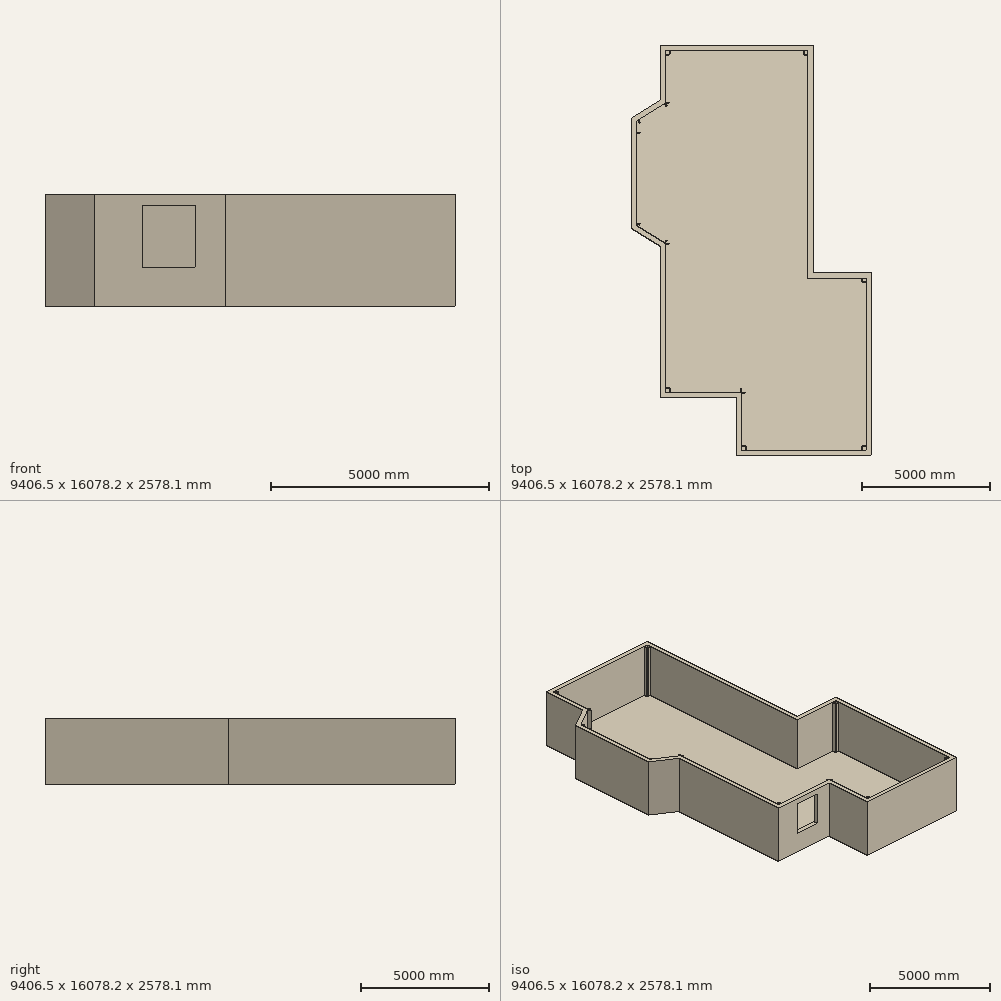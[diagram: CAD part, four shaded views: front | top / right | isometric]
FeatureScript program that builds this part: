
annotation { "Feature Type Name" : "Feature", "Feature Type Description" : "" }
export const myFeature = defineFeature(function(context is Context, id is Id, definition is map)
    precondition{}
    {
        {
            var Q0;
            Q0=qCreatedBy(makeId("Top.planeOp"),FACE);
            var sketch = newSketch(context, id + "F0", { "sketchPlane" : qUnion([Q0])});
            skLineSegment(sketch, "E0", {"start": v(-8280.4, 16078.2) * mm, "end": v(-2286, 16078.2) * mm});
            skLineSegment(sketch, "E1", {"start": v(-2286, 16078.2) * mm, "end": v(-2286, 7162.8) * mm});
            skLineSegment(sketch, "E2", {"start": v(-2286, 7162.8) * mm, "end": v(0, 7162.8) * mm});
            skLineSegment(sketch, "E3", {"start": v(0, 7162.8) * mm, "end": v(0, 0) * mm});
            skLineSegment(sketch, "E4", {"start": v(0, 0) * mm, "end": v(-5283.2, 0) * mm});
            skLineSegment(sketch, "E5", {"start": v(-5283.2, 0) * mm, "end": v(-5283.2, 2286) * mm});
            skLineSegment(sketch, "E6", {"start": v(-5283.2, 2286) * mm, "end": v(-8280.4, 2286) * mm});
            skLineSegment(sketch, "E7", {"start": v(-8280.4, 2286) * mm, "end": v(-8280.4, 8201.03) * mm});
            skLineSegment(sketch, "E8", {"start": v(-8280.4, 8201.03) * mm, "end": v(-9406.5, 8900.32) * mm});
            skLineSegment(sketch, "E9", {"start": v(-9406.5, 8900.32) * mm, "end": v(-9406.5, 13223.08) * mm});
            skLineSegment(sketch, "E10", {"start": v(-9406.5, 13223.08) * mm, "end": v(-8280.4, 13922.38) * mm});
            skLineSegment(sketch, "E11", {"start": v(-8280.4, 13922.38) * mm, "end": v(-8280.4, 16078.2) * mm});
            skSolve(sketch);
        }
        {
            var Q0;
            Q0 = qSketchRegion(id + "F0", true);
            extrude(context, id + "F1", {"entities" : qUnion([Q0]), "depth" : 2578.1 * mm});
        }
        {
            var Q0;
            Q0=makeQuery(id+"F1.opExtrude","CAP_FACE",FACE,{"disambiguationData":[OSD([sQuery(id+"F0.wireOp",EDGE,"E0"),sQuery(id+"F0.wireOp",EDGE,"E1"),sQuery(id+"F0.wireOp",EDGE,"E2"),sQuery(id+"F0.wireOp",EDGE,"E3"),sQuery(id+"F0.wireOp",EDGE,"E4"),sQuery(id+"F0.wireOp",EDGE,"E5"),sQuery(id+"F0.wireOp",EDGE,"E6"),sQuery(id+"F0.wireOp",EDGE,"E7"),sQuery(id+"F0.wireOp",EDGE,"E8"),sQuery(id+"F0.wireOp",EDGE,"E9"),sQuery(id+"F0.wireOp",EDGE,"E10"),sQuery(id+"F0.wireOp",EDGE,"E11")])],"isStart":false});
            shell(context, id + "F2", {"entities" : qUnion([Q0]), "thickness" : 203.2 * mm});
        }
        {
            var Q0;
            Q0=makeQuery(id+"F2.opShell","OFFSET_FACE",FACE,{"disambiguationData":[OSD([sQuery(id+"F0.wireOp",EDGE,"E6")])]});
            var sketch = newSketch(context, id + "F3", { "sketchPlane" : qUnion([Q0])});
            skLineSegment(sketch, "E12.bottom", {"start": v(5969, 2324.1) * mm, "end": v(7188.2, 2324.1) * mm});
            skLineSegment(sketch, "E12.top", {"start": v(5969, 901.7) * mm, "end": v(7188.2, 901.7) * mm});
            skLineSegment(sketch, "E12.left", {"start": v(5969, 2324.1) * mm, "end": v(5969, 901.7) * mm});
            skLineSegment(sketch, "E12.right", {"start": v(7188.2, 2324.1) * mm, "end": v(7188.2, 901.7) * mm});
            skPoint(sketch, "E13", {"position": v(6578.6, 2324.1) * mm});
            skSolve(sketch);
        }
        {
            var Q0;
            Q0=makeQuery(id+"F2.opShell","OFFSET_FACE",FACE,{"disambiguationData":[OSD([sQuery(id+"F0.wireOp",EDGE,"E0"),sQuery(id+"F0.wireOp",EDGE,"E1"),sQuery(id+"F0.wireOp",EDGE,"E2"),sQuery(id+"F0.wireOp",EDGE,"E3"),sQuery(id+"F0.wireOp",EDGE,"E4"),sQuery(id+"F0.wireOp",EDGE,"E5"),sQuery(id+"F0.wireOp",EDGE,"E6"),sQuery(id+"F0.wireOp",EDGE,"E7"),sQuery(id+"F0.wireOp",EDGE,"E8"),sQuery(id+"F0.wireOp",EDGE,"E9"),sQuery(id+"F0.wireOp",EDGE,"E10"),sQuery(id+"F0.wireOp",EDGE,"E11")])]});
            var sketch = newSketch(context, id + "F4", { "sketchPlane" : qUnion([Q0])});
            skLineSegment(sketch, "E14.bottom", {"start": v(-8077.2, 13811.9) * mm, "end": v(-7937.5, 13811.9) * mm});
            skLineSegment(sketch, "E14.top", {"start": v(-8077.2, 13850) * mm, "end": v(-7937.5, 13850) * mm});
            skLineSegment(sketch, "E14.left", {"start": v(-8077.2, 13811.9) * mm, "end": v(-8077.2, 13850) * mm});
            skLineSegment(sketch, "E14.right", {"start": v(-7937.5, 13811.9) * mm, "end": v(-7937.5, 13850) * mm});
            skLineSegment(sketch, "E15.bottom", {"start": v(-7934.96, 15875) * mm, "end": v(-7896.86, 15875) * mm});
            skLineSegment(sketch, "E15.top", {"start": v(-7934.96, 15735.3) * mm, "end": v(-7896.86, 15735.3) * mm});
            skLineSegment(sketch, "E15.left", {"start": v(-7934.96, 15875) * mm, "end": v(-7934.96, 15735.3) * mm});
            skLineSegment(sketch, "E15.right", {"start": v(-7896.86, 15875) * mm, "end": v(-7896.86, 15735.3) * mm});
            skLineSegment(sketch, "E16.bottom", {"start": v(-8077.2, 15694.66) * mm, "end": v(-7937.5, 15694.66) * mm});
            skLineSegment(sketch, "E16.top", {"start": v(-8077.2, 15732.76) * mm, "end": v(-7937.5, 15732.76) * mm});
            skLineSegment(sketch, "E16.left", {"start": v(-8077.2, 15694.66) * mm, "end": v(-8077.2, 15732.76) * mm});
            skLineSegment(sketch, "E16.right", {"start": v(-7937.5, 15694.66) * mm, "end": v(-7937.5, 15732.76) * mm});
            skLineSegment(sketch, "E17.bottom", {"start": v(-2631.44, 15875) * mm, "end": v(-2669.54, 15875) * mm});
            skLineSegment(sketch, "E17.top", {"start": v(-2631.44, 15735.3) * mm, "end": v(-2669.54, 15735.3) * mm});
            skLineSegment(sketch, "E17.left", {"start": v(-2631.44, 15875) * mm, "end": v(-2631.44, 15735.3) * mm});
            skLineSegment(sketch, "E17.right", {"start": v(-2669.54, 15875) * mm, "end": v(-2669.54, 15735.3) * mm});
            skLineSegment(sketch, "E18.bottom", {"start": v(-2489.2, 15694.66) * mm, "end": v(-2628.9, 15694.66) * mm});
            skLineSegment(sketch, "E18.top", {"start": v(-2489.2, 15732.76) * mm, "end": v(-2628.9, 15732.76) * mm});
            skLineSegment(sketch, "E18.left", {"start": v(-2489.2, 15694.66) * mm, "end": v(-2489.2, 15732.76) * mm});
            skLineSegment(sketch, "E18.right", {"start": v(-2628.9, 15694.66) * mm, "end": v(-2628.9, 15732.76) * mm});
            skLineSegment(sketch, "E19", {"start": v(-8078.22, 13808.73) * mm, "end": v(-8110.59, 13788.64) * mm});
            skLineSegment(sketch, "E20", {"start": v(-8110.59, 13788.64) * mm, "end": v(-8036.89, 13669.96) * mm});
            skLineSegment(sketch, "E21", {"start": v(-8036.89, 13669.96) * mm, "end": v(-8004.52, 13690.06) * mm});
            skLineSegment(sketch, "E22", {"start": v(-8004.52, 13690.06) * mm, "end": v(-8078.22, 13808.73) * mm});
            skLineSegment(sketch, "E23.bottom", {"start": v(-9203.3, 12669.47) * mm, "end": v(-9063.6, 12669.47) * mm});
            skLineSegment(sketch, "E23.top", {"start": v(-9203.3, 12631.37) * mm, "end": v(-9063.6, 12631.37) * mm});
            skLineSegment(sketch, "E23.left", {"start": v(-9203.3, 12669.47) * mm, "end": v(-9203.3, 12631.37) * mm});
            skLineSegment(sketch, "E23.right", {"start": v(-9063.6, 12669.47) * mm, "end": v(-9063.6, 12631.37) * mm});
            skLineSegment(sketch, "E24", {"start": v(-9162.3, 13135.53) * mm, "end": v(-9129.94, 13155.63) * mm});
            skLineSegment(sketch, "E25", {"start": v(-9129.94, 13155.63) * mm, "end": v(-9056.24, 13036.95) * mm});
            skLineSegment(sketch, "E26", {"start": v(-9056.24, 13036.95) * mm, "end": v(-9088.6, 13016.85) * mm});
            skLineSegment(sketch, "E27", {"start": v(-9088.6, 13016.85) * mm, "end": v(-9162.3, 13135.53) * mm});
            skLineSegment(sketch, "E28", {"start": v(-9162.3, 8987.87) * mm, "end": v(-9088.6, 9106.55) * mm});
            skLineSegment(sketch, "E29", {"start": v(-9088.6, 9106.55) * mm, "end": v(-9056.24, 9086.45) * mm});
            skLineSegment(sketch, "E30", {"start": v(-9056.24, 9086.45) * mm, "end": v(-9129.94, 8967.77) * mm});
            skLineSegment(sketch, "E31", {"start": v(-9129.94, 8967.77) * mm, "end": v(-9162.3, 8987.87) * mm});
            skLineSegment(sketch, "E32", {"start": v(-8109.57, 8334.13) * mm, "end": v(-8077.2, 8314.03) * mm});
            skLineSegment(sketch, "E33", {"start": v(-8077.2, 8314.03) * mm, "end": v(-8003.5, 8432.71) * mm});
            skLineSegment(sketch, "E34", {"start": v(-8003.5, 8432.71) * mm, "end": v(-8035.87, 8452.81) * mm});
            skLineSegment(sketch, "E35", {"start": v(-8035.87, 8452.81) * mm, "end": v(-8109.57, 8334.13) * mm});
            skLineSegment(sketch, "E36.bottom", {"start": v(-9203.3, 9061.59) * mm, "end": v(-9063.6, 9061.59) * mm});
            skLineSegment(sketch, "E36.top", {"start": v(-9203.3, 9099.69) * mm, "end": v(-9063.6, 9099.69) * mm});
            skLineSegment(sketch, "E36.left", {"start": v(-9203.3, 9061.59) * mm, "end": v(-9203.3, 9099.69) * mm});
            skLineSegment(sketch, "E36.right", {"start": v(-9063.6, 9061.59) * mm, "end": v(-9063.6, 9099.69) * mm});
            skLineSegment(sketch, "E37.bottom", {"start": v(-8077.2, 8311.5) * mm, "end": v(-7937.5, 8311.5) * mm});
            skLineSegment(sketch, "E37.top", {"start": v(-8077.2, 8273.4) * mm, "end": v(-7937.5, 8273.4) * mm});
            skLineSegment(sketch, "E37.left", {"start": v(-8077.2, 8311.5) * mm, "end": v(-8077.2, 8273.4) * mm});
            skLineSegment(sketch, "E37.right", {"start": v(-7937.5, 8311.5) * mm, "end": v(-7937.5, 8273.4) * mm});
            skLineSegment(sketch, "E38.bottom", {"start": v(-8077.2, 2631.44) * mm, "end": v(-7937.5, 2631.44) * mm});
            skLineSegment(sketch, "E38.top", {"start": v(-8077.2, 2669.54) * mm, "end": v(-7937.5, 2669.54) * mm});
            skLineSegment(sketch, "E38.left", {"start": v(-8077.2, 2631.44) * mm, "end": v(-8077.2, 2669.54) * mm});
            skLineSegment(sketch, "E38.right", {"start": v(-7937.5, 2631.44) * mm, "end": v(-7937.5, 2669.54) * mm});
            skLineSegment(sketch, "E39.bottom", {"start": v(-7896.86, 2489.2) * mm, "end": v(-7934.96, 2489.2) * mm});
            skLineSegment(sketch, "E39.top", {"start": v(-7896.86, 2628.9) * mm, "end": v(-7934.96, 2628.9) * mm});
            skLineSegment(sketch, "E39.left", {"start": v(-7896.86, 2489.2) * mm, "end": v(-7896.86, 2628.9) * mm});
            skLineSegment(sketch, "E39.right", {"start": v(-7934.96, 2489.2) * mm, "end": v(-7934.96, 2628.9) * mm});
            skLineSegment(sketch, "E40.bottom", {"start": v(-5082.54, 2489.2) * mm, "end": v(-5120.64, 2489.2) * mm});
            skLineSegment(sketch, "E40.top", {"start": v(-5082.54, 2628.9) * mm, "end": v(-5120.64, 2628.9) * mm});
            skLineSegment(sketch, "E40.left", {"start": v(-5082.54, 2489.2) * mm, "end": v(-5082.54, 2628.9) * mm});
            skLineSegment(sketch, "E40.right", {"start": v(-5120.64, 2489.2) * mm, "end": v(-5120.64, 2628.9) * mm});
            skLineSegment(sketch, "E41.top", {"start": v(-5080, 2448.56) * mm, "end": v(-4940.3, 2448.56) * mm});
            skLineSegment(sketch, "E41.right", {"start": v(-4940.3, 2486.66) * mm, "end": v(-4940.3, 2448.56) * mm});
            skLineSegment(sketch, "E42.bottom", {"start": v(-5080, 345.44) * mm, "end": v(-4940.3, 345.44) * mm});
            skLineSegment(sketch, "E42.top", {"start": v(-5080, 383.54) * mm, "end": v(-4940.3, 383.54) * mm});
            skLineSegment(sketch, "E42.left", {"start": v(-5080, 345.44) * mm, "end": v(-5080, 383.54) * mm});
            skLineSegment(sketch, "E42.right", {"start": v(-4940.3, 345.44) * mm, "end": v(-4940.3, 383.54) * mm});
            skLineSegment(sketch, "E43.bottom", {"start": v(-4937.76, 203.2) * mm, "end": v(-4899.66, 203.2) * mm});
            skLineSegment(sketch, "E43.top", {"start": v(-4937.76, 342.9) * mm, "end": v(-4899.66, 342.9) * mm});
            skLineSegment(sketch, "E43.left", {"start": v(-4937.76, 203.2) * mm, "end": v(-4937.76, 342.9) * mm});
            skLineSegment(sketch, "E43.right", {"start": v(-4899.66, 203.2) * mm, "end": v(-4899.66, 342.9) * mm});
            skLineSegment(sketch, "E44.bottom", {"start": v(-383.54, 203.2) * mm, "end": v(-345.44, 203.2) * mm});
            skLineSegment(sketch, "E44.top", {"start": v(-383.54, 342.9) * mm, "end": v(-345.44, 342.9) * mm});
            skLineSegment(sketch, "E44.left", {"start": v(-383.54, 203.2) * mm, "end": v(-383.54, 342.9) * mm});
            skLineSegment(sketch, "E44.right", {"start": v(-345.44, 203.2) * mm, "end": v(-345.44, 342.9) * mm});
            skLineSegment(sketch, "E45.bottom", {"start": v(-203.2, 345.44) * mm, "end": v(-342.9, 345.44) * mm});
            skLineSegment(sketch, "E45.top", {"start": v(-203.2, 383.54) * mm, "end": v(-342.9, 383.54) * mm});
            skLineSegment(sketch, "E45.left", {"start": v(-203.2, 345.44) * mm, "end": v(-203.2, 383.54) * mm});
            skLineSegment(sketch, "E45.right", {"start": v(-342.9, 345.44) * mm, "end": v(-342.9, 383.54) * mm});
            skLineSegment(sketch, "E46.bottom", {"start": v(-203.2, 6779.26) * mm, "end": v(-342.9, 6779.26) * mm});
            skLineSegment(sketch, "E46.top", {"start": v(-203.2, 6817.36) * mm, "end": v(-342.9, 6817.36) * mm});
            skLineSegment(sketch, "E46.left", {"start": v(-203.2, 6779.26) * mm, "end": v(-203.2, 6817.36) * mm});
            skLineSegment(sketch, "E46.right", {"start": v(-342.9, 6779.26) * mm, "end": v(-342.9, 6817.36) * mm});
            skLineSegment(sketch, "E47.bottom", {"start": v(-345.44, 6959.6) * mm, "end": v(-383.54, 6959.6) * mm});
            skLineSegment(sketch, "E47.top", {"start": v(-345.44, 6819.9) * mm, "end": v(-383.54, 6819.9) * mm});
            skLineSegment(sketch, "E47.left", {"start": v(-345.44, 6959.6) * mm, "end": v(-345.44, 6819.9) * mm});
            skLineSegment(sketch, "E47.right", {"start": v(-383.54, 6959.6) * mm, "end": v(-383.54, 6819.9) * mm});
            skLineSegment(sketch, "E48", {"start": v(-4940.3, 2486.66) * mm, "end": v(-5080, 2486.66) * mm});
            skLineSegment(sketch, "E49", {"start": v(-5080, 2486.66) * mm, "end": v(-5080, 2448.56) * mm});
            skLineSegment(sketch, "E50", {"start": v(-9203.3, 13110.07) * mm, "end": v(-9045.7, 12987.43) * mm, "construction": true});
            skLineSegment(sketch, "E51", {"start": v(-9045.7, 12987.43) * mm, "end": v(-9104.83, 13171.22) * mm, "construction": true});
            skLineSegment(sketch, "E52", {"start": v(-9104.83, 13171.22) * mm, "end": v(-9203.3, 12968.55) * mm, "construction": true});
            skLineSegment(sketch, "E53", {"start": v(-9203.3, 12968.55) * mm, "end": v(-9045.7, 12987.43) * mm, "construction": true});
            skSolve(sketch);
        }
        {
            var Q0;
            Q0 = qSketchRegion(id + "F3", true);
            var Q1;
            Q1=makeQuery(id+"F7.opExtrude","SWEPT_FACE",FACE,{"disambiguationData":[OSD([sQuery(id+"FoojXG4nMktDod7_1.wireOp",EDGE,"1VciS72g-VBcj-X035-P1CE-B9HJ2LFSvZOH.top"),sQuery(id+"FoojXG4nMktDod7_1.wireOp",EDGE,"icQnHHDd-8pVd-SaWu-tjJm-3fqmfHu7QenC")])]});
            extrude(context, id + "F5", {"entities" : qUnion([Q0]), "operationType" : NewBodyOperationType.REMOVE, "endBound" : BoundingType.UP_TO_NEXT, "oppositeDirection" : true, "depth" : 25.4 * mm});
        }
        {
            var Q0;
            Q0 = qSketchRegion(id + "F4", true);
            extrude(context, id + "F6", {"entities" : qUnion([Q0]), "operationType" : NewBodyOperationType.ADD, "depth" : 2349.5 * mm});
        }
    });
